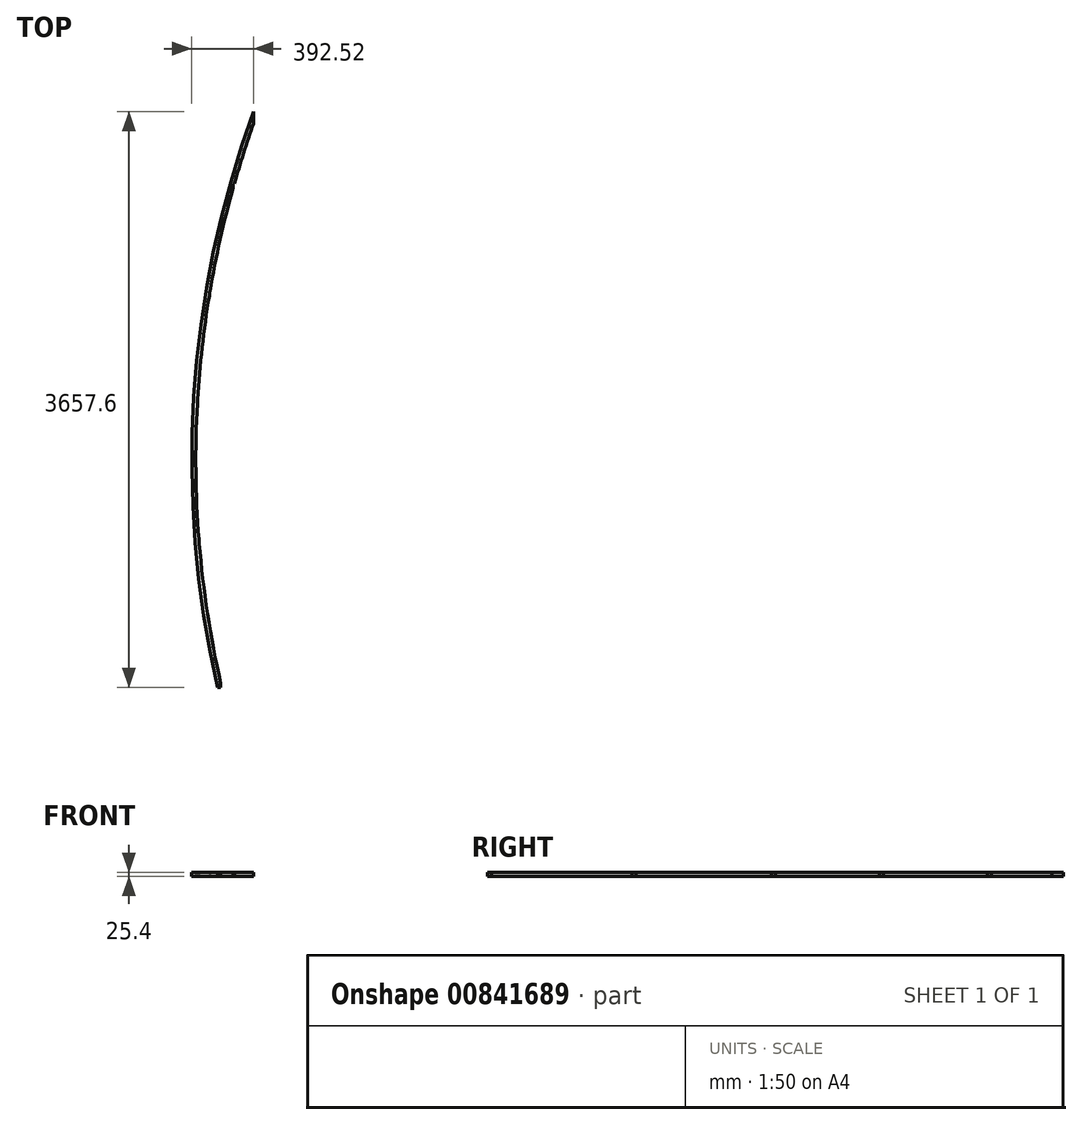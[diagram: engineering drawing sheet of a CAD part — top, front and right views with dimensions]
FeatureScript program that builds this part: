
annotation { "Feature Type Name" : "Feature", "Feature Type Description" : "" }
export const myFeature = defineFeature(function(context is Context, id is Id, definition is map)
    precondition{}
    {
        {
            var Q0;
            Q0=qCreatedBy(makeId("Top.planeOp"),FACE);
            var sketch = newSketch(context, id + "F0", { "sketchPlane" : qUnion([Q0])});
            skLineSegment(sketch, "E0", {"start": v(0, 0) * mm, "end": v(0, 1828.8) * mm, "construction": true});
            skLineSegment(sketch, "E1", {"start": v(0, 0) * mm, "end": v(0, -1828.8) * mm, "construction": true});
            skLineSegment(sketch, "E2", {"start": v(0, 0) * mm, "end": v(-381, 0) * mm, "construction": true});
            skLineSegment(sketch, "E3", {"start": v(0, -1828.8) * mm, "end": v(-202.53, -1828.8) * mm, "construction": true});
            skArc(sketch, "E4", {"start": v(0, 1828.8) * mm, "mid": v(-379.98, 16.6) * mm, "end": v(-228.6, -1828.8) * mm});
            skArc(sketch, "E5.0", {"start": v(0, 1753.8) * mm, "mid": v(-63.93, 1563.65) * mm, "end": v(-121.88, 1371.6) * mm});
            skLineSegment(sketch, "E6", {"start": v(0, 1828.8) * mm, "end": v(0, 1753.8) * mm});
            skLineSegment(sketch, "E7", {"start": v(-228.6, -1828.8) * mm, "end": v(-208.35, -1828.8) * mm});
            skLineSegment(sketch, "E8", {"start": v(-208.35, -1803.4) * mm, "end": v(-208.35, -1828.8) * mm});
            skLineSegment(sketch, "E9.trimOffspring", {"start": v(-208.35, -1828.8) * mm, "end": v(-228.6, -1828.8) * mm, "construction": true});
            skLineSegment(sketch, "E10", {"start": v(-129.06, 1346.2) * mm, "end": v(-129.06, 1371.6) * mm});
            skLineSegment(sketch, "E11", {"start": v(-129.06, 1371.6) * mm, "end": v(-121.88, 1371.6) * mm});
            skArc(sketch, "E12.trimOffspring", {"start": v(-129.06, 1346.2) * mm, "mid": v(-211.8, 1017.95) * mm, "end": v(-277.1, 685.8) * mm});
            skLineSegment(sketch, "E13", {"start": v(-357.03, -25.4) * mm, "end": v(-357.03, 0) * mm});
            skLineSegment(sketch, "E14", {"start": v(-357.03, 0) * mm, "end": v(-355.55, 0) * mm});
            skArc(sketch, "E15.trimOffspring", {"start": v(-357.03, -25.4) * mm, "mid": v(-366.72, -456.9) * mm, "end": v(-347.37, -888.07) * mm});
            skLineSegment(sketch, "E16", {"start": v(-208.35, -1803.4) * mm, "end": v(-202.53, -901.7) * mm, "construction": true});
            skLineSegment(sketch, "E17", {"start": v(-202.53, -901.7) * mm, "end": v(-208.35, 0) * mm, "construction": true});
            skLineSegment(sketch, "E18", {"start": v(-202.53, -901.7) * mm, "end": v(-347.37, -900.77) * mm, "construction": true});
            skPoint(sketch, "E18.endSnap0", {"position": v(-347.37, -888.07) * mm});
            skLineSegment(sketch, "E19", {"start": v(-347.37, -888.07) * mm, "end": v(-347.37, -913.47) * mm});
            skLineSegment(sketch, "E20", {"start": v(-347.37, -913.47) * mm, "end": v(-345.32, -913.47) * mm});
            skArc(sketch, "E21.trimOffspring", {"start": v(-345.32, -913.47) * mm, "mid": v(-292.47, -1360.84) * mm, "end": v(-208.35, -1803.4) * mm});
            skLineSegment(sketch, "E22", {"start": v(-129.06, 1346.2) * mm, "end": v(-129.06, 673.1) * mm, "construction": true});
            skLineSegment(sketch, "E23", {"start": v(-129.06, 673.1) * mm, "end": v(-129.06, 0) * mm, "construction": true});
            skLineSegment(sketch, "E24", {"start": v(-129.06, 673.1) * mm, "end": v(-281.35, 673.1) * mm, "construction": true});
            skLineSegment(sketch, "E25", {"start": v(-281.35, 685.8) * mm, "end": v(-281.35, 660.4) * mm});
            skLineSegment(sketch, "E26", {"start": v(-281.35, 685.8) * mm, "end": v(-277.1, 685.8) * mm});
            skArc(sketch, "E27.trimOffspring", {"start": v(-281.35, 660.4) * mm, "mid": v(-327, 331.16) * mm, "end": v(-355.55, 0) * mm});
            skLineSegment(sketch, "E28", {"start": v(-129.06, 1358.9) * mm, "end": v(0, 1358.9) * mm, "construction": true});
            skLineSegment(sketch, "E29", {"start": v(-281.35, 673.1) * mm, "end": v(0, 673.1) * mm, "construction": true});
            skLineSegment(sketch, "E30", {"start": v(-357.03, -12.7) * mm, "end": v(0, -12.7) * mm, "construction": true});
            skLineSegment(sketch, "E31", {"start": v(-347.37, -900.77) * mm, "end": v(0, -900.77) * mm, "construction": true});
            skSolve(sketch);
        }
        {
            var Q0;
            Q0 = qSketchRegion(id + "F0", true);
            extrude(context, id + "F1", {"entities" : qUnion([Q0]), "depth" : 25.4 * mm, "offsetDistance" : 25.4 * mm});
        }
    });
